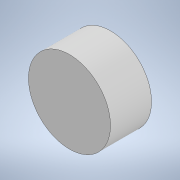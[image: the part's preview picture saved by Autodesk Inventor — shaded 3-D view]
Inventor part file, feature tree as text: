
AUTODESK INVENTOR PART (.ipt)
format: ipt  version: 2021 (Build 250183000, 183)  size: 91,648 bytes
history: native  units: mm
features: other x1, extrude x1, sketch x1
ambient origin geometry x8: Origin, YZ Plane, XZ Plane, XY Plane, X Axis, Y Axis, Z Axis, Center Point
bodies: Body1 (feature_tree)
feature tree (3):
  other  "Sólido1"
  extrude  "Extrusión1"  Depth=30.0mm TaperAngle=0.0deg
  sketch  "Boceto1"  dims[d0=60.0mm d1=30.0mm d2=0.0mm]
